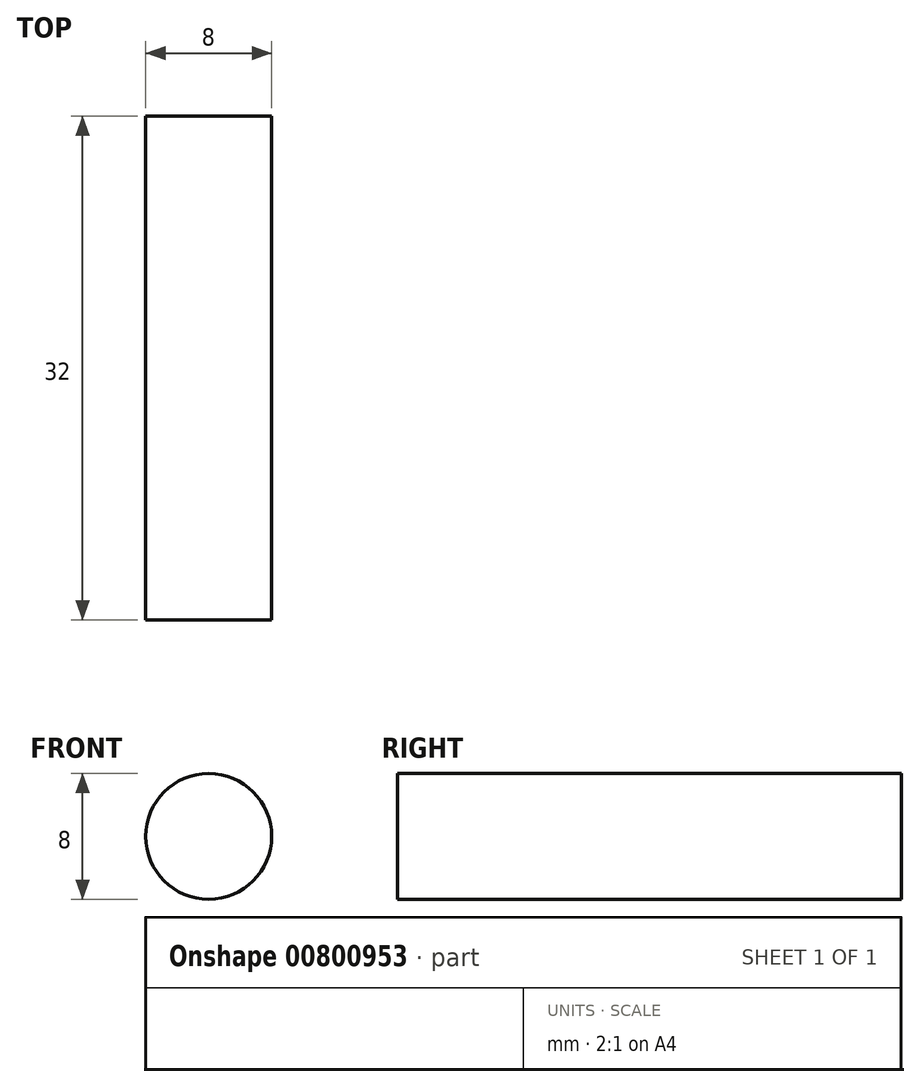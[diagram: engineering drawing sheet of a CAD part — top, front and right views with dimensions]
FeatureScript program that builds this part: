
annotation { "Feature Type Name" : "Feature", "Feature Type Description" : "" }
export const myFeature = defineFeature(function(context is Context, id is Id, definition is map)
    precondition{}
    {
        {
            var Q0;
            Q0=qCreatedBy(makeId("Top.planeOp"),FACE);
            var sketch = newSketch(context, id + "F0", { "sketchPlane" : qUnion([Q0])});
            skLineSegment(sketch, "E0.bottom", {"start": v(0, 0) * mm, "end": v(4, 0) * mm});
            skLineSegment(sketch, "E0.top", {"start": v(0, -32) * mm, "end": v(4, -32) * mm});
            skLineSegment(sketch, "E0.left", {"start": v(0, 0) * mm, "end": v(0, -32) * mm});
            skLineSegment(sketch, "E0.right", {"start": v(4, 0) * mm, "end": v(4, -32) * mm});
            skSolve(sketch);
        }
        {
            var Q0;
            Q0=makeQuery(id+"F0.imprint","IMPRINT",FACE,{"disambiguationData":[TD([[makeQuery(id+"F0.imprint","IMPRINT",EDGE,{"derivedFrom":sQuery(id+"F0.wireOp",EDGE,"E0.bottom")}),-1.0]])]});
            var Q1;
            Q1=sQuery(id+"F0.wireOp",EDGE,"E0.left");
            revolve(context, id + "F1", {"surfaceOperationType" : NewSurfaceOperationType.NEW, "entities" : qUnion([Q0]), "axis" : qUnion([Q1]), "revolveType" : RevolveType.FULL});
        }
    });
